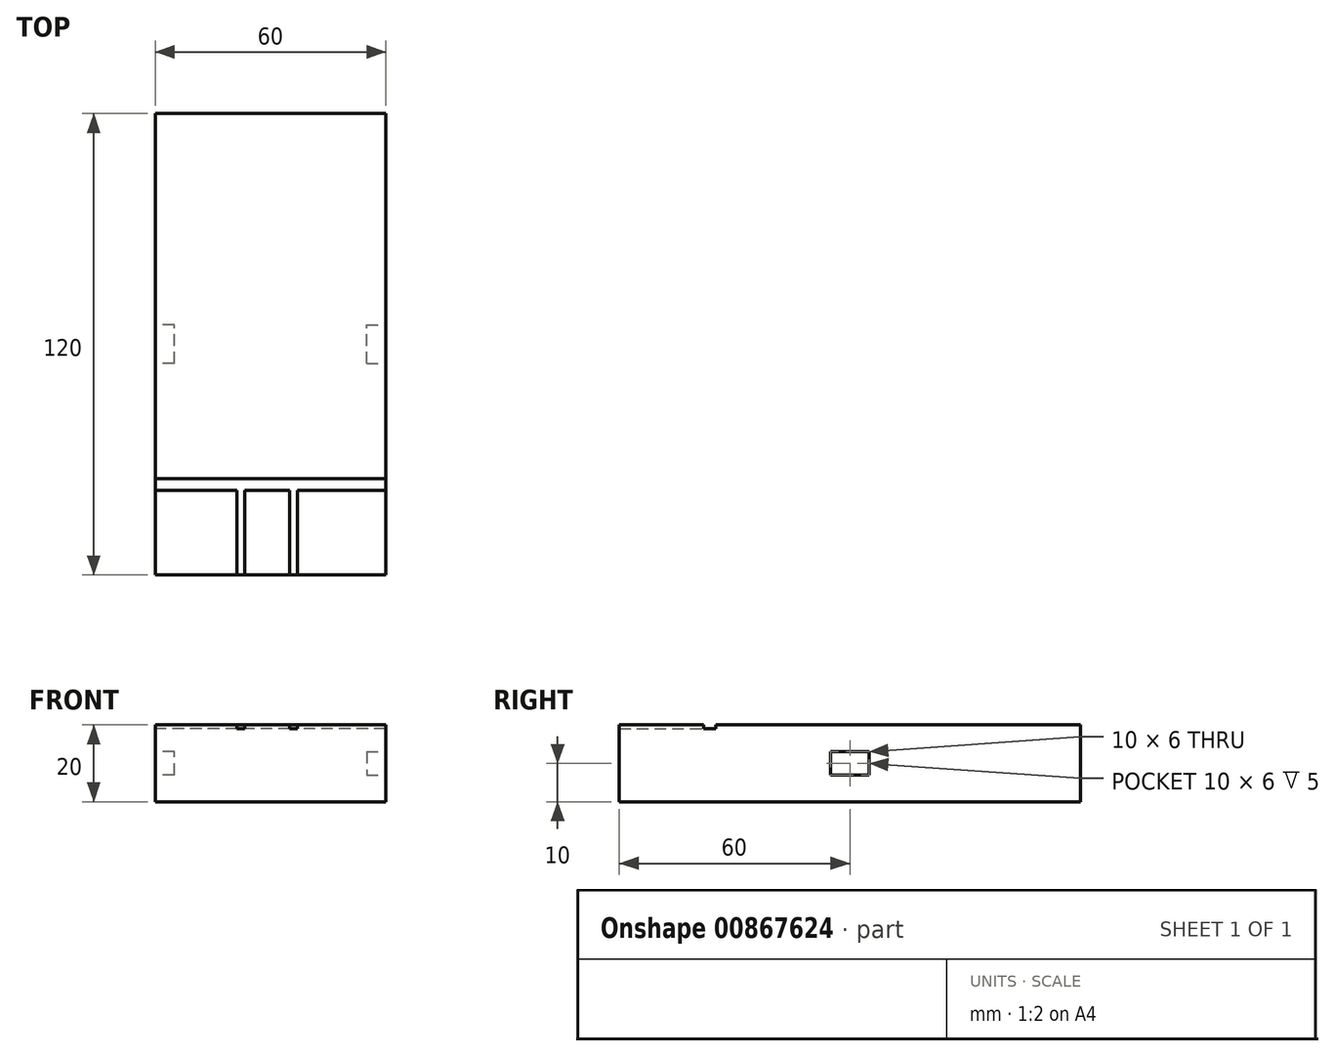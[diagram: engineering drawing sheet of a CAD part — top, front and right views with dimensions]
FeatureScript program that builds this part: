
annotation { "Feature Type Name" : "Feature", "Feature Type Description" : "" }
export const myFeature = defineFeature(function(context is Context, id is Id, definition is map)
    precondition{}
    {
        {
            var Q0;
            Q0=qCreatedBy(makeId("Front.planeOp"),FACE);
            var sketch = newSketch(context, id + "F0", { "sketchPlane" : qUnion([Q0])});
            skLineSegment(sketch, "E0", {"start": v(0, 0) * mm, "end": v(0, 20) * mm});
            skLineSegment(sketch, "E1", {"start": v(0, 20) * mm, "end": v(60, 20) * mm});
            skLineSegment(sketch, "E2", {"start": v(60, 20) * mm, "end": v(60, 0) * mm});
            skLineSegment(sketch, "E3", {"start": v(60, 0) * mm, "end": v(0, 0) * mm});
            skSolve(sketch);
        }
        {
            var Q0;
            Q0=makeQuery(id+"F0.imprint","IMPRINT",FACE,{"disambiguationData":[TD([[makeQuery(id+"F0.imprint","IMPRINT",EDGE,{"derivedFrom":sQuery(id+"F0.wireOp",EDGE,"E0")}),-1.0]])]});
            extrude(context, id + "F1", {"entities" : qUnion([Q0]), "depth" : 120 * mm, "offsetDistance" : 25 * mm});
        }
        {
            var Q0;
            Q0=makeQuery(id+"F1.opExtrude","SWEPT_FACE",FACE,{"disambiguationData":[OSD([sQuery(id+"F0.wireOp",EDGE,"E1")])]});
            var sketch = newSketch(context, id + "F2", { "sketchPlane" : qUnion([Q0])});
            skLineSegment(sketch, "E4.bottom", {"start": v(60, -98.06) * mm, "end": v(0, -98.06) * mm});
            skLineSegment(sketch, "E4.top", {"start": v(60, -94.94) * mm, "end": v(0, -94.94) * mm});
            skLineSegment(sketch, "E4.left", {"start": v(60, -98.06) * mm, "end": v(60, -94.94) * mm});
            skLineSegment(sketch, "E4.right", {"start": v(0, -98.06) * mm, "end": v(0, -94.94) * mm});
            skSolve(sketch);
        }
        {
            var Q0;
            Q0=makeQuery(id+"F2.imprint","IMPRINT",FACE,{"disambiguationData":[TD([[makeQuery(id+"F2.imprint","IMPRINT",EDGE,{"derivedFrom":sQuery(id+"F2.wireOp",EDGE,"E4.bottom")}),-1.0]])]});
            extrude(context, id + "F3", {"entities" : qUnion([Q0]), "operationType" : NewBodyOperationType.REMOVE, "oppositeDirection" : true, "depth" : 1 * mm, "offsetDistance" : 25 * mm});
        }
        {
            var Q0;
            {var subQ2=sQuery(id+"F0.wireOp",EDGE,"E1");Q0=makeQuery(id+"F3.boolean.opBoolean","SPLIT",FACE,{"disambiguationData":[TD([makeQuery(id+"F3.opExtrude","SWEPT_FACE",FACE,{"disambiguationData":[OSD([sQuery(id+"F2.wireOp",EDGE,"E4.bottom")])]})])],"derivedFrom":makeQuery(id+"F1.opExtrude","SWEPT_FACE",FACE,{"disambiguationData":[OSD([subQ2])]})});}
            var sketch = newSketch(context, id + "F4", { "sketchPlane" : qUnion([Q0])});
            skLineSegment(sketch, "E5.bottom", {"start": v(37.02, -120) * mm, "end": v(35.02, -120) * mm});
            skLineSegment(sketch, "E5.top", {"start": v(37.02, -98.06) * mm, "end": v(35.02, -98.06) * mm});
            skLineSegment(sketch, "E5.left", {"start": v(37.02, -120) * mm, "end": v(37.02, -98.06) * mm});
            skLineSegment(sketch, "E5.right", {"start": v(35.02, -120) * mm, "end": v(35.02, -98.06) * mm});
            skLineSegment(sketch, "E6.bottom", {"start": v(23.29, -120) * mm, "end": v(21.29, -120) * mm});
            skLineSegment(sketch, "E6.top", {"start": v(23.29, -98.06) * mm, "end": v(21.29, -98.06) * mm});
            skLineSegment(sketch, "E6.left", {"start": v(23.29, -120) * mm, "end": v(23.29, -98.06) * mm});
            skLineSegment(sketch, "E6.right", {"start": v(21.29, -120) * mm, "end": v(21.29, -98.06) * mm});
            skSolve(sketch);
        }
        {
            var Q0;
            Q0=makeQuery(id+"F4.imprint","IMPRINT",FACE,{"disambiguationData":[TD([[makeQuery(id+"F4.imprint","IMPRINT",EDGE,{"derivedFrom":sQuery(id+"F4.wireOp",EDGE,"E5.bottom")}),1.0]])]});
            var Q1;
            Q1=makeQuery(id+"F4.imprint","IMPRINT",FACE,{"disambiguationData":[TD([[makeQuery(id+"F4.imprint","IMPRINT",EDGE,{"derivedFrom":sQuery(id+"F4.wireOp",EDGE,"E6.bottom")}),1.0]])]});
            extrude(context, id + "F5", {"entities" : qUnion([Q0, Q1]), "operationType" : NewBodyOperationType.REMOVE, "oppositeDirection" : true, "depth" : 1 * mm, "offsetDistance" : 25 * mm});
        }
        {
            var Q0;
            Q0=makeQuery(id+"F1.opExtrude","SWEPT_FACE",FACE,{"disambiguationData":[OSD([sQuery(id+"F0.wireOp",EDGE,"E2")])]});
            var sketch = newSketch(context, id + "F6", { "sketchPlane" : qUnion([Q0])});
            skLineSegment(sketch, "E7.bottom", {"start": v(-65, 13) * mm, "end": v(-55, 13) * mm});
            skLineSegment(sketch, "E7.top", {"start": v(-65, 7) * mm, "end": v(-55, 7) * mm});
            skLineSegment(sketch, "E7.left", {"start": v(-65, 13) * mm, "end": v(-65, 7) * mm});
            skLineSegment(sketch, "E7.right", {"start": v(-55, 13) * mm, "end": v(-55, 7) * mm});
            skSolve(sketch);
        }
        {
            var Q0;
            Q0=makeQuery(id+"F6.imprint","IMPRINT",FACE,{"disambiguationData":[TD([[makeQuery(id+"F6.imprint","IMPRINT",EDGE,{"derivedFrom":sQuery(id+"F6.wireOp",EDGE,"E7.bottom")}),-1.0]])]});
            extrude(context, id + "F7", {"entities" : qUnion([Q0]), "operationType" : NewBodyOperationType.REMOVE, "oppositeDirection" : true, "depth" : 5 * mm, "offsetDistance" : 25 * mm});
        }
        {
            var Q0;
            Q0=makeQuery(id+"F1.opExtrude","SWEPT_FACE",FACE,{"disambiguationData":[OSD([sQuery(id+"F0.wireOp",EDGE,"E0")])]});
            var sketch = newSketch(context, id + "F8", { "sketchPlane" : qUnion([Q0])});
            skLineSegment(sketch, "E8.bottom", {"start": v(65, 7) * mm, "end": v(55, 7) * mm});
            skLineSegment(sketch, "E8.top", {"start": v(65, 13) * mm, "end": v(55, 13) * mm});
            skLineSegment(sketch, "E8.left", {"start": v(65, 7) * mm, "end": v(65, 13) * mm});
            skLineSegment(sketch, "E8.right", {"start": v(55, 7) * mm, "end": v(55, 13) * mm});
            skSolve(sketch);
        }
        {
            var Q0;
            Q0=makeQuery(id+"F8.imprint","IMPRINT",FACE,{"disambiguationData":[TD([[makeQuery(id+"F8.imprint","IMPRINT",EDGE,{"derivedFrom":sQuery(id+"F8.wireOp",EDGE,"E8.bottom")}),-1.0]])]});
            extrude(context, id + "F9", {"entities" : qUnion([Q0]), "operationType" : NewBodyOperationType.REMOVE, "oppositeDirection" : true, "depth" : 5 * mm, "offsetDistance" : 25 * mm});
        }
    });
